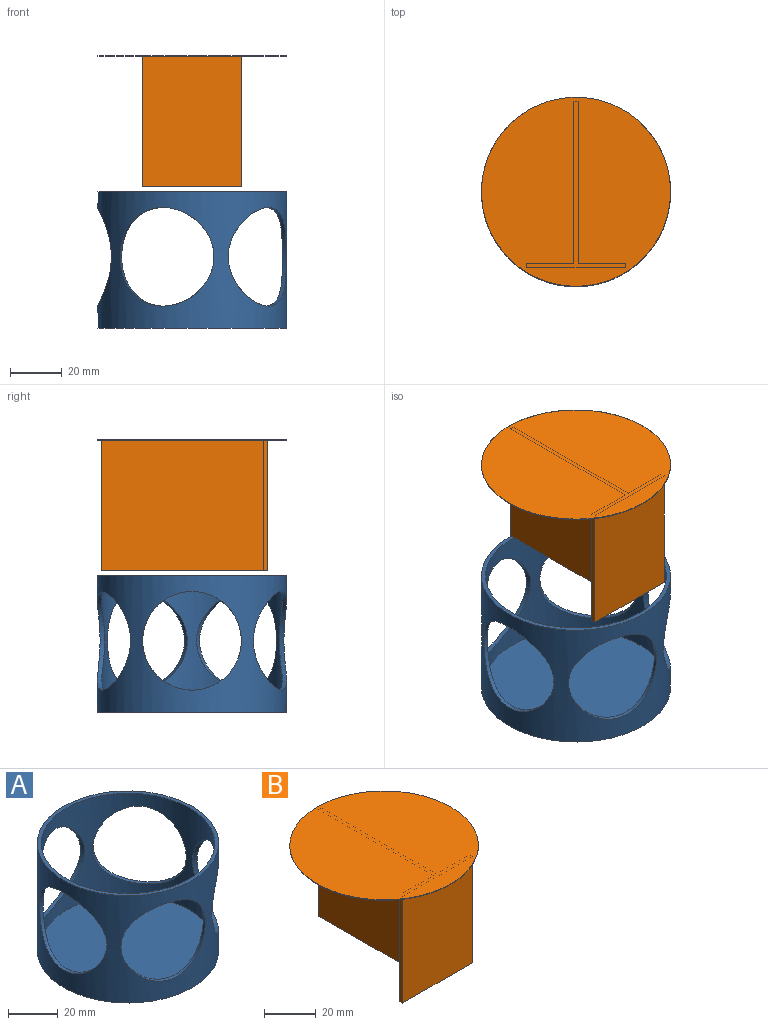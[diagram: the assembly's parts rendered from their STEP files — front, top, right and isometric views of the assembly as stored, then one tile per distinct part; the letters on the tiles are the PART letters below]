
ASSEMBLY  parts=2 mates=1
PART A: 10 faces, bbox 77.3x81.2x52.8 mm
  f0: cylinder r=34.92mm len=69.85mm, axis (0,0,-1), area 5087.1mm2, adj f2,f3,f4,f5,f6,f7,f8
  f1: cylinder r=36.51mm len=73.03mm, axis (0,0,-1), area 6192mm2, adj f2,f3,f4,f5,f6,f7,f9
  f2: plane 73.03x73.03mm, normal (0,0,1), area 356.3mm2, adj f0,f1
  f3: cylinder r=19.05mm len=38.1mm, axis (1,0,0), area 205.9mm2, adj f0,f1
  f4: cylinder r=19.05mm len=38.47mm, axis (0.31,-0.95,0), area 206.5mm2, adj f0,f1
  f5: cylinder r=19.05mm len=38.1mm, axis (-0.81,-0.59,0), area 206.5mm2, adj f0,f1
  f6: cylinder r=19.05mm len=38.1mm, axis (-0.81,0.59,0), area 206.5mm2, adj f0,f1
  f7: cylinder r=19.05mm len=38.47mm, axis (0.31,0.95,0), area 206.5mm2, adj f0,f1
  f8: plane 69.85x69.85mm, normal (0,0,1), area 3832mm2, adj f0
  f9: plane 73.03x73.03mm, normal (0,0,-1), area 4188.3mm2, adj f1
PART B: 12 faces, bbox 73x73x50.5 mm
  f0: cylinder r=34.92mm len=50.29mm, axis (0,0,-1), area 79.8mm2, adj f1,f3,f4,f9
  f1: plane 73.03x73.03mm, normal (0,0,-1), area 4028.4mm2, adj f0,f2,f3,f4,f5,f6,f7,f8
  f2: plane 50.29x18.26mm, normal (0,1,0), area 918.1mm2, adj f1,f3,f8,f9
  f3: plane 62.6x50.29mm, normal (-1,0,0), area 3148.3mm2, adj f0,f1,f2,f9
  f4: plane 62.6x50.29mm, normal (1,0,0), area 3148.3mm2, adj f0,f1,f5,f9
  f5: plane 50.29x18.26mm, normal (0,1,0), area 918.1mm2, adj f1,f4,f6,f9
  f6: plane 50.29x1.59mm, normal (1,0,0), area 79.8mm2, adj f1,f5,f7,f9
  f7: plane 50.29x38.1mm, normal (0,-1,0), area 1916.1mm2, adj f1,f6,f8,f9
  f8: plane 50.29x1.59mm, normal (-1,0,0), area 79.8mm2, adj f1,f2,f7,f9
  f9: plane 64.2x38.1mm, normal (0,0,-1), area 159.9mm2, adj f0,f2,f3,f4,f5,f6,f7,f8
  f10: cylinder r=36.51mm len=73.03mm, axis (0,0,1), area 58.3mm2, adj f1,f11
  f11: plane 73.03x73.03mm, normal (0,0,1), area 4188.3mm2, adj f10
PLACE A t=(-134.35,64.76,52.36)mm
PLACE B t=(-134.35,64.76,154.97)mm
MATE cylindrical B.f10 <-> A.f0  axis (0,0,1) through (-134.35,64.76,155.23)mm
